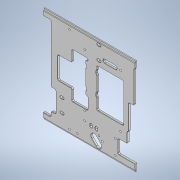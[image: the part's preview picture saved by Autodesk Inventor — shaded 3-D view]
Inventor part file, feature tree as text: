
AUTODESK INVENTOR PART (.ipt)
format: ipt  version: 2021 (Build 250183000, 183)  size: 777,728 bytes
history: native  units: mm
features: extrude x21, sketch x19, reference x18, other x9, fillet x6, thicken_offset x6, projected_geometry x3, chamfer x1
ambient origin geometry x8: Origin, YZ Plane, XZ Plane, XY Plane, X Axis, Y Axis, Z Axis, Center Point
bodies: Solid1 (feature_tree)
feature tree (83):
  extrude  "Extrusion1"  Depth=150.0mm
  extrude  "Extrusion2"  Depth=10.0mm
  extrude  "Extrusion3"  Depth=10.0mm
  extrude  "Extrusion4"  Depth=14.903711mm
  extrude  "Extrusion5"  Depth=33.425867mm
  extrude  "Extrusion6"  Depth=8.898mm
  extrude  "Extrusion7"  Depth=19.598mm
  extrude  "Extrusion8"  Depth=49.0mm
  extrude  "Extrusion9"  Depth=34.0mm
  extrude  "Extrusion10"  Depth=4.0mm
  extrude  "Extrusion11"  Depth=47.0mm
  extrude  "Extrusion12"  Depth=27.0mm
  extrude  "Extrusion13"  Depth=5.5mm
  extrude  "Extrusion14"  Depth=5.0mm TaperAngle=0.0deg
  fillet  "Fillet1"  Radius=3.0mm
  fillet  "Fillet2"  Radius=3.0mm
  fillet  "Fillet3"  Radius=1.2mm
  extrude  "Extrusion15"  Depth=67.0mm
  extrude  "Extrusion16"  TaperAngle=0.0deg  [1 undecoded]
  fillet  "Fillet4"  [1 undecoded]
  extrude  "Extrusion17"  Depth=10.0mm
  thicken_offset  "Thicken1"
  thicken_offset  "Thicken2"
  thicken_offset  "Thicken3"
  thicken_offset  "Thicken4"
  extrude  "Extrusion18"  TaperAngle=0.0deg  [1 undecoded]
  thicken_offset  "Thicken5"
  thicken_offset  "Thicken6"
  extrude  "Extrusion19"  Depth=12.0mm
  fillet  "Fillet5"  Radius=22.0mm
  extrude  "Extrusion20"  TaperAngle=0.0deg  [1 undecoded]
  fillet  "Fillet6"  Radius=36.0mm
  extrude  "Extrusion21"  Depth=8.0mm
  chamfer  "Chamfer1"  [1 undecoded]
  sketch  "Sketch1"  dims[d0=150.0mm d1=156.0mm]
  sketch  "Sketch2"  dims[d2=1.8mm d3=0.0mm d4=10.0mm]
  projected_geometry  "Projected Loop1"
  sketch  "Sketch4"  dims[d5=10.0mm d6=13.0mm]
  reference  "Reference1"
  reference  "Reference2"
  reference  "Reference3"
  reference  "Reference4"
  sketch  "Sketch5"  dims[d7=0.0mm d8=0.0mm d9=14.903711mm]
  sketch  "Sketch6"  dims[d10=14.90369mm d11=33.425867mm]
  sketch  "Sketch7"  dims[d12=5.537mm d13=8.898mm]
  reference  "Reference7"
  reference  "Reference8"
  reference  "Reference9"
  reference  "Reference10"
  reference  "Reference11"
  reference  "Reference12"
  sketch  "Sketch8"  dims[d14=23.737mm d15=19.598mm]
  projected_geometry  "Projected Loop2"
  sketch  "Sketch9"  dims[d16=0.0mm d17=0.0mm d18=49.0mm]
  sketch  "Sketch10"  dims[d19=77.0mm d20=34.0mm]
  reference  "Reference13"
  reference  "Reference14"
  reference  "Reference15"
  reference  "Reference16"
  reference  "Reference17"
  reference  "Reference18"
  sketch  "Sketch11"  dims[d22=10.0mm d23=0.0mm d24=4.0mm]
  reference  "Reference19"
  sketch  "Sketch12"  dims[d25=69.0mm d26=47.0mm]
  reference  "Reference20"
  sketch  "Sketch13"  dims[d27=30.0mm d28=27.0mm]
  sketch  "Sketch15"  dims[d30=22.0mm d31=5.5mm]
  sketch  "Sketch16"  dims[d32=10.0mm d33=0.0mm d34=5.0mm d35=0.0mm d36=3.0mm d37=3.0mm d38=1.2mm d39=0.0mm]
  projected_geometry  "Projected Loop3"
  sketch  "Sketch18"  dims[d40=53.0mm d41=67.0mm]
  sketch  "Sketch19"  dims[d42=23.0mm d43=0.0mm d44=0.0mm d45=0.0mm d46=0.0mm]
  sketch  "Sketch21"  dims[d47=10.0mm d48=10.0mm]
  sketch  "Sketch22"  dims[d50=2.0mm d51=0.0mm d52=0.0mm]
  sketch  "Sketch23"  dims[d53=53.0mm d54=12.0mm d55=22.0mm d56=0.0mm d57=0.0mm d58=36.0mm d59=8.0mm d60=0.0mm d61=0.0mm d62=34.0mm d63=8.0mm d64=0.0mm d65=0.0mm d66=6.0mm d67=3.5mm d68=3.5mm d70=6.0mm d71=59.0mm d72=6.0mm d73=3.5mm d74=3.5mm d75=18.0mm d77=10.0mm d78=0.0mm d79=0.0mm d80=2.0mm d81=1.75mm d82=2.0mm d83=10.0mm d84=10.0mm d85=12.75mm d86=63.5mm d87=0.0mm d88=0.0mm d89=3.0mm d90=3.0mm d91=3.0mm d94=3.0mm d95=3.0mm d96=3.0mm d97=3.0mm d98=3.0mm d99=3.0mm d100=3.0mm d101=0.0mm d102=0.0mm d103=2.0mm d104=18.0mm d105=2.0mm d106=0.5mm d107=0.5mm d108=0.0mm d109=0.0mm d110=0.25mm d111=0.25mm d112=0.25mm d113=0.25mm d114=0.25mm d115=0.25mm d116=0.25mm d117=0.25mm d118=15.0mm d119=34.0mm d120=6.25mm d121=6.0mm d122=3.5mm d125=10.0mm d126=0.0mm d127=5.0mm d128=90.0deg d130=10.0mm d131=5.0mm d132=3.75mm d133=3.75mm d134=3.0mm d135=0.05mm d136=0.05mm d137=0.05mm d138=0.05mm d139=9.0mm d140=6.0mm d141=4.0mm d142=4.0mm d143=4.0mm d144=0.0mm d145=0.0mm d146=2.0mm d147=18.0mm d148=1.5mm d149=1.5mm d150=6.0mm d151=6.0mm d152=3.650067mm d153=3.650067mm d154=0.0mm d155=0.0mm d156=2.0mm d157=1.75mm d158=1.75mm d159=2.5mm d160=2.5mm d161=5.0mm d162=0.0mm d163=35.0mm d164=18.0mm d165=10.0mm d166=0.0mm d167=0.5mm d168=2.0mm d169=45.0deg d171=22.0mm d172=10.0mm d174=6.0mm d175=6.0mm]
  other  "<userpath>\Google Drive\Unicorn 2020\CAD\Assembly.iam"
  other  "Assembly.iam"
  other  "Jetson_Nano_Dev_Kit_3D_b01:1"
  other  "682-13450_PORG_ME_THER_ASSY:1"
  other  "USB_MAIN_PCB:1"
  other  "IO_HEADER_PCB_ASS:1"
  other  "IO_HEADER_PCB:1"
  other  "84161000_ABD-1600_Back:1"
  other  "DI 1600:1"
note: 5 required parameter values undecoded (feature->parameter linkage not recoverable at this tier; creation-order binding heuristic only, values carry confidence <= 0.55)
